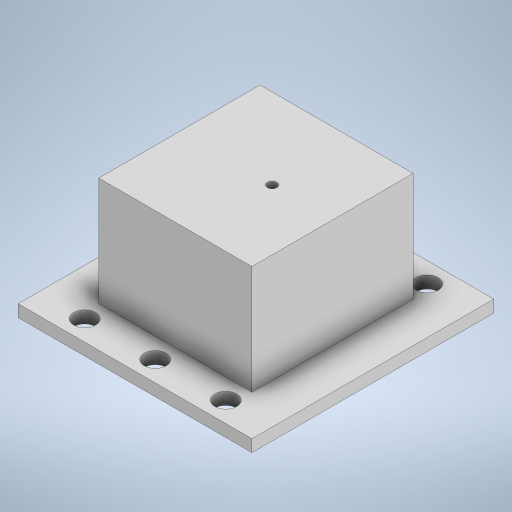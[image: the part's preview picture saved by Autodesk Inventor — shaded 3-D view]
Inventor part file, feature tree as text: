
AUTODESK INVENTOR PART (.ipt)
format: ipt  version: 2024 (Build 280153000, 153)  size: 321,024 bytes
history: native  units: mm
features: extrude x7, sketch x7, plane x3
ambient origin geometry x8: Origin, YZ Plane, XZ Plane, XY Plane, X Axis, Y Axis, Z Axis, Center Point
bodies: Body1 (feature_tree)
feature tree (17):
  plane  "Work Plane5"
  extrude  "Extrusion34"  Depth=40.0mm
  plane  "Work Plane2"
  extrude  "Extrusion35"  Depth=30.0mm
  plane  "Work Plane1"
  extrude  "Extrusion51"  Depth=30.0mm
  sketch  "Sketch77"  dims[d211=10.0mm d212=0.0mm d219=35.0mm]
  extrude  "Extrusion53"  Depth=10.0mm
  extrude  "Extrusion54"  Depth=60.0mm
  extrude  "Extrusion56"  Depth=3.0mm TaperAngle=0.0deg
  extrude  "Extrusion57"  Depth=4.5mm
  sketch  "Sketch45"  dims[d142=38.0mm d143=40.0mm]
  sketch  "Sketch47"  dims[d144=30.0mm d145=0.0mm d146=36.0mm]
  sketch  "Sketch74"  dims[d147=30.0mm d148=-2.617994mm d210=2.3mm]
  sketch  "Sketch78"  dims[d220=58.0mm d221=60.0mm]
  sketch  "Sketch81"  dims[d222=3.0mm d223=0.0mm d224=3.0mm d225=0.0mm]
  sketch  "Sketch83"  dims[d232=5.0mm d233=11.5mm d234=5.4mm d235=17.5mm d236=5.4mm d237=17.5mm d238=5.4mm d239=5.0mm d240=17.0mm d241=5.4mm d242=16.0mm d243=5.4mm d244=17.0mm d245=5.4mm d246=17.5mm d247=5.4mm d248=17.5mm d249=5.0mm d250=30.0mm d251=0.0mm d253=5.0mm d254=4.5mm d255=0.0mm d49=0.5mm d50=0.872665mm d51=0.5mm d52=0.872665mm d130=0.5mm d131=0.872665mm d132=0.5mm d133=0.872665mm d156=0.5mm d157=0.872665mm d158=0.5mm d159=0.872665mm d173=0.5mm d174=0.872665mm d175=0.5mm d176=0.872665mm d226=0.5mm d227=0.872665mm]
